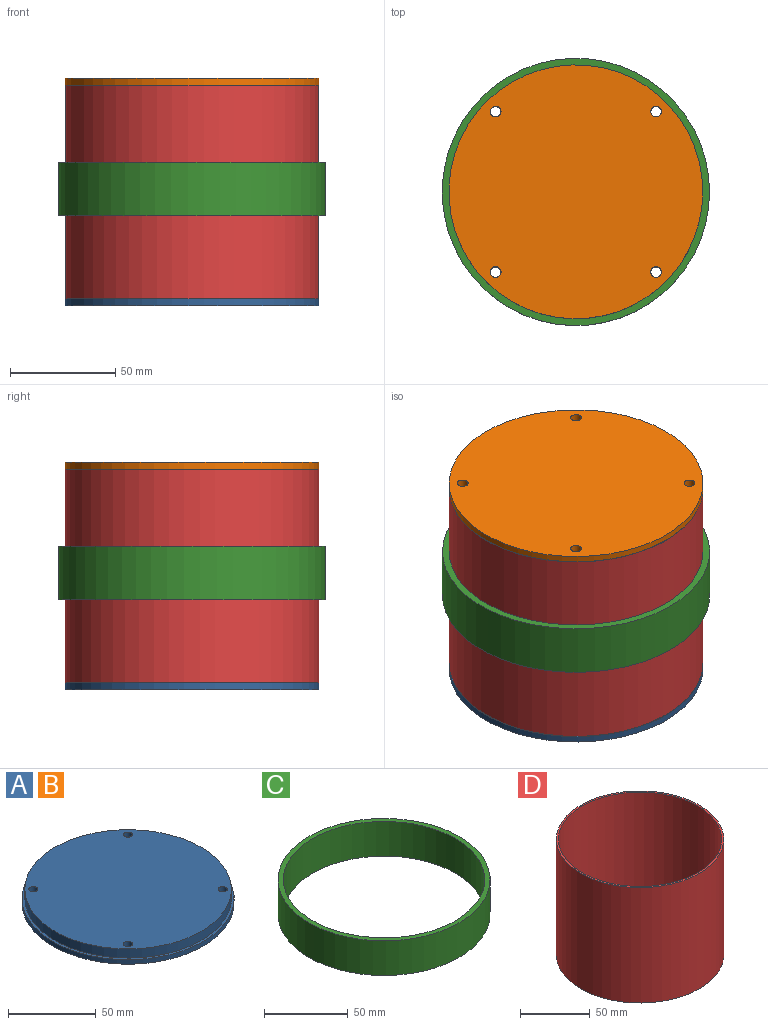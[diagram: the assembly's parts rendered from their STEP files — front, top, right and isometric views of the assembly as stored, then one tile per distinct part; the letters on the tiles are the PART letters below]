
ASSEMBLY  parts=4 mates=3
PART A: 9 faces, bbox 120.7x120.7x9.5 mm
  f0: cylinder r=60.32mm len=120.65mm, axis (0,0,-1), area 1203.4mm2, adj f1,f2
  f1: plane 120.65x120.65mm, normal (0,0,1), area 593.8mm2, adj f0,f3
  f2: plane 120.65x120.65mm, normal (0,0,-1), area 11350.7mm2, adj f0,f5,f6,f7,f8
  f3: cylinder r=58.74mm len=117.48mm, axis (0,0,-1), area 2343.5mm2, adj f1,f4
  f4: plane 117.48x117.48mm, normal (0,0,1), area 10756.9mm2, adj f3,f5,f6,f7,f8
  f5: cylinder r=2.55mm len=9.53mm, axis (0,0,-1), area 152.8mm2, adj f2,f4
  f6: cylinder r=2.55mm len=9.53mm, axis (0,0,-1), area 152.8mm2, adj f2,f4
  f7: cylinder r=2.55mm len=9.53mm, axis (0,0,-1), area 152.8mm2, adj f2,f4
  f8: cylinder r=2.55mm len=9.53mm, axis (0,0,-1), area 152.8mm2, adj f2,f4
PART B: same geometry as A
PART C: 4 faces, bbox 127x127x25.4 mm
  f0: cylinder r=60.32mm len=120.65mm, axis (0,0,-1), area 9627.4mm2, adj f2,f3
  f1: cylinder r=63.5mm len=127mm, axis (0,0,-1), area 10134.1mm2, adj f2,f3
  f2: plane 127x127mm, normal (0,0,1), area 1235.1mm2, adj f0,f1
  f3: plane 127x127mm, normal (0,0,-1), area 1235.1mm2, adj f0,f1
PART D: 4 faces, bbox 120.4x120.4x101.6 mm
  f0: cylinder r=58.74mm len=117.48mm, axis (0,0,-1), area 37496.4mm2, adj f2,f3
  f1: cylinder r=60.2mm len=120.4mm, axis (0,0,-1), area 38428.7mm2, adj f2,f3
  f2: plane 120.4x120.4mm, normal (0,0,1), area 545.7mm2, adj f0,f1
  f3: plane 120.4x120.4mm, normal (0,0,-1), area 545.7mm2, adj f0,f1
PLACE A t=(-10.9,-21.88,36.32)mm
PLACE B rot(axis=(1,0,0),180deg) t=(-10.9,-21.88,144.27)mm
PLACE C t=(-10.9,-21.88,79.1)mm
PLACE D t=(-10.9,-21.88,39.5)mm
MATE revolute B.f0 <-> D.f0  axis (0,0,-1) through (-10.9,-21.88,141.1)mm
MATE revolute A.f0 <-> D.f0  axis (0,0,1) through (-10.9,-21.88,39.5)mm
MATE slider C.f0 <-> D.f0  axis (0,0,-1) through (-10.9,-21.88,91.8)mm
